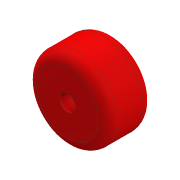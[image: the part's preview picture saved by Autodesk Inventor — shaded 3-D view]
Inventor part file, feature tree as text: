
AUTODESK INVENTOR PART (.ipt)
format: ipt  version: 2020 (Build 240168000, 168)  size: 127,488 bytes
history: native  units: mm
features: other x1, extrude x1, fillet x1, sketch x1
ambient origin geometry x8: Origin, YZ Plane, XZ Plane, XY Plane, X Axis, Y Axis, Z Axis, Center Point
bodies: Body1 (feature_tree)
feature tree (4):
  other  "솔리드1"
  extrude  "돌출1"  Depth=25.0mm
  fillet  "모깎기1"  Radius=5.0mm
  sketch  "스케치1"
